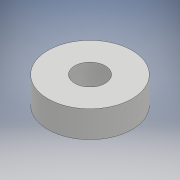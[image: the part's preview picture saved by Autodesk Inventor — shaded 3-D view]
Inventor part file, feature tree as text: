
AUTODESK INVENTOR PART (.ipt)
format: ipt  version: 2017 (Build 210142000, 142)  size: 94,720 bytes
history: native  units: mm
features: extrude x1, sketch x1
ambient origin geometry x8: Origin, YZ Plane, XZ Plane, XY Plane, X Axis, Y Axis, Z Axis, Center Point
bodies: Solid1 (feature_tree)
feature tree (2):
  extrude  "Extrusion1"  Depth=7.0mm
  sketch  "Sketch1"  dims[d0=8.0mm d1=22.0mm d2=7.0mm d3=0.0mm]
